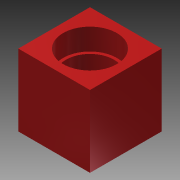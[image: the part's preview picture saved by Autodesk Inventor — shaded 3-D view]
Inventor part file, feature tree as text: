
AUTODESK INVENTOR PART (.ipt)
format: ipt  version: 2014 (Build 180170000, 170)  size: 107,008 bytes
history: native  units: mm
features: sketch x3, extrude x2, plane x2, revolve x1, projected_geometry x1
ambient origin geometry x8: Origin, YZ Plane, XZ Plane, XY Plane, X Axis, Y Axis, Z Axis, Center Point
bodies: Solid1 (feature_tree)
feature tree (9):
  extrude  "Extrusion1"  Depth=30.0mm
  plane  "Work Plane1"
  plane  "Work Plane2"
  extrude  "Extrusion2"  [1 undecoded]
  revolve  "Revolution1"  [1 undecoded]
  sketch  "Sketch1"  dims[d0=22.5mm d1=30.0mm]
  sketch  "Sketch2"  dims[d2=30.0mm d3=0.0mm d4=-9.0mm]
  sketch  "Sketch3"  dims[d5=-9.0mm d6=20.0mm d7=30.0mm d8=0.0mm d9=45.0deg d10=90.0deg]
  projected_geometry  "Project Cut Edges1"
note: 2 required parameter values undecoded (feature->parameter linkage not recoverable at this tier; creation-order binding heuristic only, values carry confidence <= 0.55)